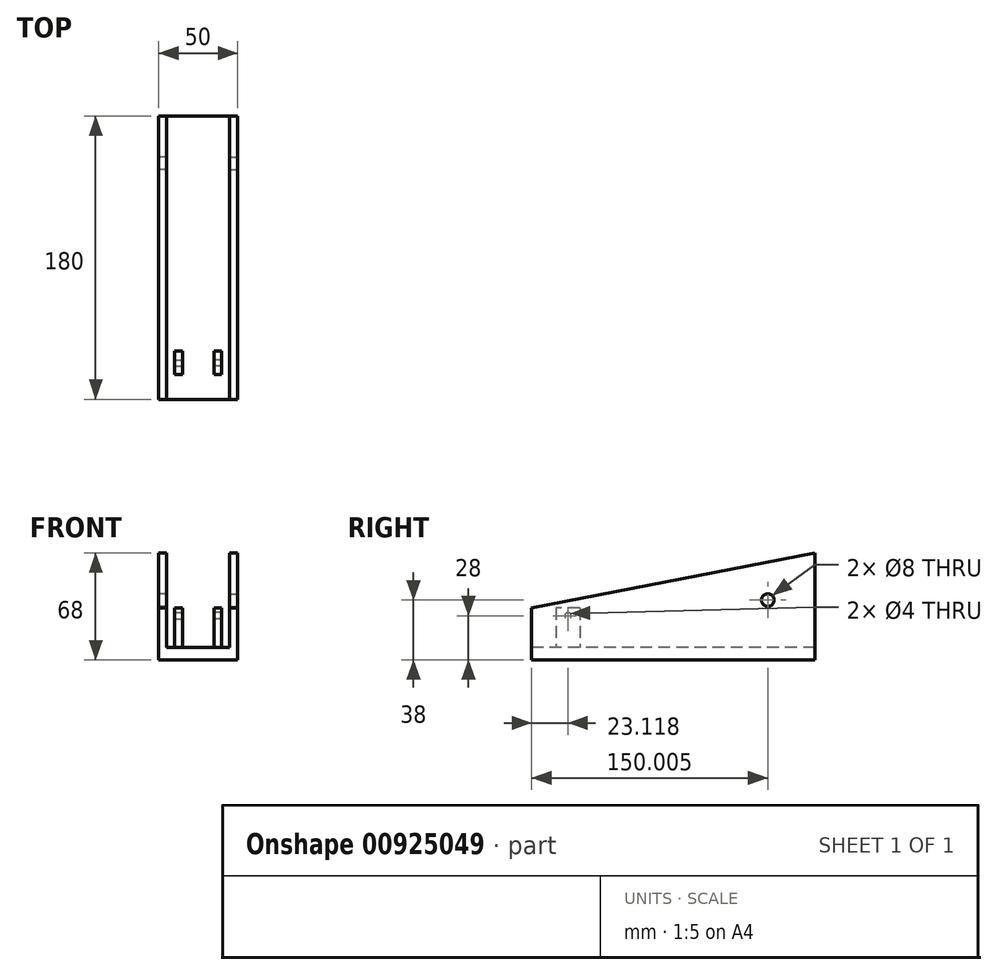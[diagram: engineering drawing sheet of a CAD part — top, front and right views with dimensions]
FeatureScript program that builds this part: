
annotation { "Feature Type Name" : "Feature", "Feature Type Description" : "" }
export const myFeature = defineFeature(function(context is Context, id is Id, definition is map)
    precondition{}
    {
        {
            var Q0;
            Q0=qCreatedBy(makeId("Top.planeOp"),FACE);
            var sketch = newSketch(context, id + "F0", { "sketchPlane" : qUnion([Q0])});
            skLineSegment(sketch, "E0.bottom", {"start": v(-27.45, 74.86) * mm, "end": v(22.55, 74.86) * mm});
            skLineSegment(sketch, "E0.top", {"start": v(-27.45, -105.14) * mm, "end": v(22.55, -105.14) * mm});
            skLineSegment(sketch, "E0.left", {"start": v(-27.45, 74.86) * mm, "end": v(-27.45, -105.14) * mm});
            skLineSegment(sketch, "E0.right", {"start": v(22.55, 74.86) * mm, "end": v(22.55, -105.14) * mm});
            skSolve(sketch);
        }
        {
            var Q0;
            Q0=makeQuery(id+"F0.imprint","IMPRINT",FACE,{"disambiguationData":[TD([[makeQuery(id+"F0.imprint","IMPRINT",EDGE,{"derivedFrom":sQuery(id+"F0.wireOp",EDGE,"E0.bottom")}),-1.0]])]});
            extrude(context, id + "F1", {"entities" : qUnion([Q0]), "oppositeDirection" : true, "depth" : 8 * mm, "offsetDistance" : 25 * mm});
        }
        {
            var Q0;
            Q0=makeQuery(id+"F1.opExtrude","SWEPT_FACE",FACE,{"disambiguationData":[OSD([sQuery(id+"F0.wireOp",EDGE,"E0.left")])]});
            var sketch = newSketch(context, id + "F2", { "sketchPlane" : qUnion([Q0])});
            skLineSegment(sketch, "E1", {"start": v(-74.86, 0) * mm, "end": v(-74.86, 60) * mm});
            skLineSegment(sketch, "E2", {"start": v(105.14, 0) * mm, "end": v(105.14, 25) * mm});
            skLineSegment(sketch, "E3", {"start": v(105.14, 25) * mm, "end": v(-74.86, 60) * mm});
            skLineSegment(sketch, "E4", {"start": v(-74.86, 0) * mm, "end": v(105.14, 0) * mm});
            skCircle(sketch, "E5", {"center": v(-44.86, 30) * mm, "radius": 4 * mm});
            skSolve(sketch);
        }
        {
            var Q0;
            Q0=makeQuery(id+"F2.imprint","IMPRINT",FACE,{"disambiguationData":[TD([[makeQuery(id+"F2.imprint","IMPRINT",EDGE,{"derivedFrom":sQuery(id+"F2.wireOp",EDGE,"E1")}),-1.0]])]});
            extrude(context, id + "F3", {"entities" : qUnion([Q0]), "operationType" : NewBodyOperationType.ADD, "oppositeDirection" : true, "depth" : 5 * mm, "offsetDistance" : 25 * mm});
        }
        {
            var Q0;
            Q0=makeQuery(id+"F1.opExtrude","SWEPT_FACE",FACE,{"disambiguationData":[OSD([sQuery(id+"F0.wireOp",EDGE,"E0.right")])]});
            var sketch = newSketch(context, id + "F4", { "sketchPlane" : qUnion([Q0])});
            skLineSegment(sketch, "E6", {"start": v(-105.14, 0) * mm, "end": v(-105.14, 25) * mm});
            skLineSegment(sketch, "E7", {"start": v(-105.14, 25) * mm, "end": v(74.86, 60) * mm});
            skLineSegment(sketch, "E8", {"start": v(74.86, 60) * mm, "end": v(74.86, 0) * mm});
            skLineSegment(sketch, "E9", {"start": v(74.86, 0) * mm, "end": v(-105.14, 0) * mm});
            skCircle(sketch, "E10", {"center": v(44.86, 30) * mm, "radius": 4 * mm});
            skSolve(sketch);
        }
        {
            var Q0;
            Q0=qSketchRegion(id+"F4",true);
            extrude(context, id + "F5", {"entities" : qUnion([Q0]), "operationType" : NewBodyOperationType.ADD, "oppositeDirection" : true, "depth" : 5 * mm, "offsetDistance" : 25 * mm});
        }
        {
            var Q0;
            Q0=makeQuery(id+"F1.opExtrude","CAP_FACE",FACE,{"disambiguationData":[OSD([sQuery(id+"F0.wireOp",EDGE,"E0.bottom"),sQuery(id+"F0.wireOp",EDGE,"E0.top"),sQuery(id+"F0.wireOp",EDGE,"E0.left"),sQuery(id+"F0.wireOp",EDGE,"E0.right")])],"isStart":true});
            var sketch = newSketch(context, id + "F6", { "sketchPlane" : qUnion([Q0])});
            skLineSegment(sketch, "E11.bottom", {"start": v(-17.45, -74.52) * mm, "end": v(-12.45, -74.52) * mm});
            skLineSegment(sketch, "E11.top", {"start": v(-17.45, -89.52) * mm, "end": v(-12.45, -89.52) * mm});
            skLineSegment(sketch, "E11.left", {"start": v(-17.45, -74.52) * mm, "end": v(-17.45, -89.52) * mm});
            skLineSegment(sketch, "E11.right", {"start": v(-12.45, -74.52) * mm, "end": v(-12.45, -89.52) * mm});
            skLineSegment(sketch, "E12.bottom", {"start": v(7.55, -74.53) * mm, "end": v(12.55, -74.53) * mm});
            skLineSegment(sketch, "E12.top", {"start": v(7.55, -89.53) * mm, "end": v(12.55, -89.53) * mm});
            skLineSegment(sketch, "E12.left", {"start": v(7.55, -74.53) * mm, "end": v(7.55, -89.53) * mm});
            skLineSegment(sketch, "E12.right", {"start": v(12.55, -74.53) * mm, "end": v(12.55, -89.53) * mm});
            skSolve(sketch);
        }
        {
            var Q0;
            Q0=makeQuery(id+"F6.imprint","IMPRINT",FACE,{"disambiguationData":[TD([[makeQuery(id+"F6.imprint","IMPRINT",EDGE,{"derivedFrom":sQuery(id+"F6.wireOp",EDGE,"E11.bottom")}),-1.0]])]});
            var Q1;
            Q1=makeQuery(id+"F6.imprint","IMPRINT",FACE,{"disambiguationData":[TD([[makeQuery(id+"F6.imprint","IMPRINT",EDGE,{"derivedFrom":sQuery(id+"F6.wireOp",EDGE,"E12.bottom")}),-1.0]])]});
            extrude(context, id + "F7", {"entities" : qUnion([Q0, Q1]), "operationType" : NewBodyOperationType.ADD, "depth" : 25 * mm, "offsetDistance" : 25 * mm});
        }
        {
            var Q0;
            Q0=makeQuery(id+"F7.opExtrude","SWEPT_FACE",FACE,{"disambiguationData":[OSD([sQuery(id+"F6.wireOp",EDGE,"E11.right")])]});
            var sketch = newSketch(context, id + "F8", { "sketchPlane" : qUnion([Q0])});
            skCircle(sketch, "E13", {"center": v(-82.02, 20) * mm, "radius": 2 * mm});
            skSolve(sketch);
        }
        {
            var Q0;
            Q0=makeQuery(id+"F8.imprint","IMPRINT",FACE,{"disambiguationData":[TD([[makeQuery(id+"F8.imprint","IMPRINT",EDGE,{"derivedFrom":sQuery(id+"F8.wireOp",EDGE,"E13")}),1.0]])]});
            extrude(context, id + "F9", {"entities" : qUnion([Q0]), "operationType" : NewBodyOperationType.REMOVE, "oppositeDirection" : true, "depth" : 5 * mm, "offsetDistance" : 25 * mm});
        }
        {
            var Q0;
            Q0=makeQuery(id+"F7.opExtrude","SWEPT_FACE",FACE,{"disambiguationData":[OSD([sQuery(id+"F6.wireOp",EDGE,"E12.left")])]});
            var sketch = newSketch(context, id + "F10", { "sketchPlane" : qUnion([Q0])});
            skCircle(sketch, "E14", {"center": v(82.02, 20) * mm, "radius": 2 * mm});
            skSolve(sketch);
        }
        {
            var Q0;
            Q0=makeQuery(id+"F10.imprint","IMPRINT",FACE,{"disambiguationData":[TD([[makeQuery(id+"F10.imprint","IMPRINT",EDGE,{"derivedFrom":sQuery(id+"F10.wireOp",EDGE,"E14")}),1.0]])]});
            extrude(context, id + "F11", {"entities" : qUnion([Q0]), "operationType" : NewBodyOperationType.REMOVE, "oppositeDirection" : true, "depth" : 5 * mm, "offsetDistance" : 25 * mm});
        }
    });
